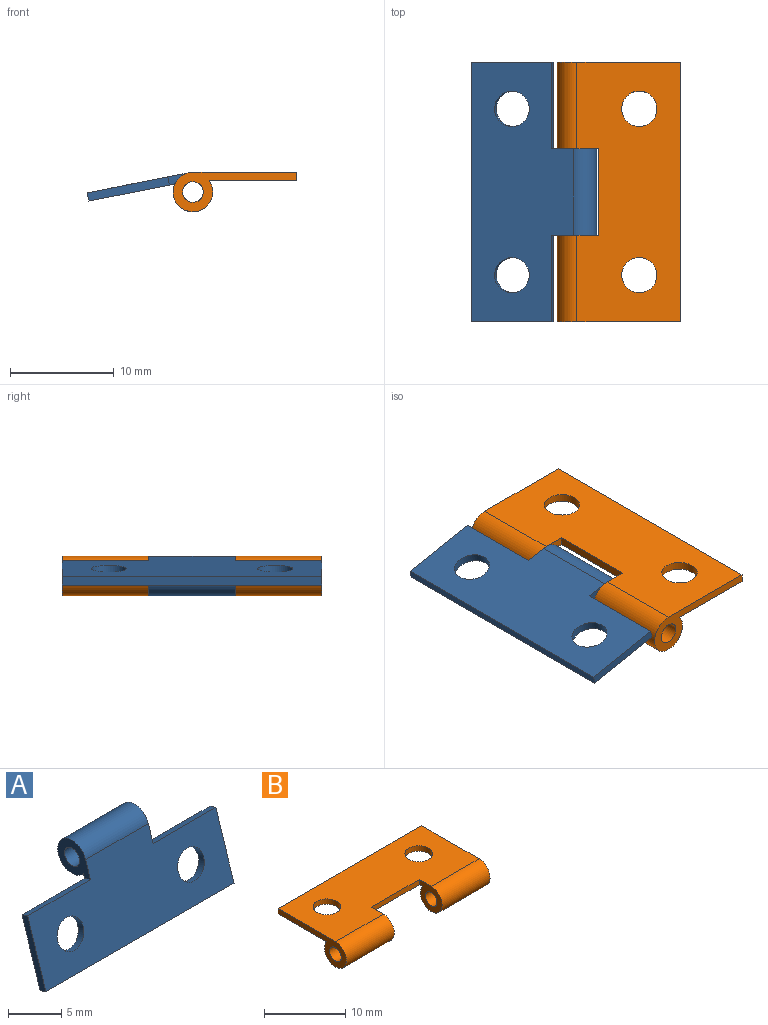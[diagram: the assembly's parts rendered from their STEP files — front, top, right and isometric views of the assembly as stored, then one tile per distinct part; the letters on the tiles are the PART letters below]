
ASSEMBLY  parts=2 mates=1
PART A: 13 faces, bbox 25x6.8x11.1 mm
  f0: cylinder r=1.9mm len=8.33mm, axis (1,0,0), area 84.4mm2, adj f1,f2,f6,f8
  f1: plane 25x8.05mm, normal (0,0.95,-0.31), area 184.1mm2, adj f0,f3,f4,f5,f6,f7,f8,f9
  f2: plane 25x9.52mm, normal (0,-0.95,0.31), area 197mm2, adj f0,f3,f4,f5,f6,f7,f8,f9
  f3: plane 7.78x3.18mm, normal (-1,0,0), area 6.3mm2, adj f1,f2,f5,f7
  f4: plane 7.78x3.18mm, normal (1,0,0), area 6.3mm2, adj f1,f2,f5,f9
  f5: plane 25x0.76mm, normal (0,-0.31,-0.95), area 20mm2, adj f1,f2,f3,f4
  f6: plane 4.35x3.8mm, normal (-1,0,0), area 9mm2, adj f0,f1,f2,f7,f10
  f7: plane 8.33x0.76mm, normal (0,0.31,0.95), area 6.7mm2, adj f1,f2,f3,f6
  f8: plane 4.35x3.8mm, normal (1,0,0), area 9mm2, adj f0,f1,f2,f9,f10
  f9: plane 8.33x0.76mm, normal (0,0.31,0.95), area 6.7mm2, adj f1,f2,f4,f8
  f10: cylinder r=1mm len=8.33mm, axis (1,0,0), area 52.4mm2, adj f6,f8
  f11: cylinder r=1.7mm len=3.48mm, axis (0,-0.95,0.31), area 8.5mm2, adj f1,f2
  f12: cylinder r=1.7mm len=3.48mm, axis (0,-0.95,0.31), area 8.5mm2, adj f1,f2
PART B: 14 faces, bbox 25x11.9x3.8 mm
  f0: plane 25x8.45mm, normal (0,0,-1), area 188.6mm2, adj f1,f2,f6,f7,f8,f9,f10,f11
  f1: cylinder r=1.9mm len=8.33mm, axis (1,0,0), area 84.4mm2, adj f0,f3,f7,f9
  f2: cylinder r=1.9mm len=8.33mm, axis (1,0,0), area 84.4mm2, adj f0,f3,f8,f10
  f3: plane 25x10mm, normal (0,0,1), area 214.4mm2, adj f1,f2,f6,f7,f8,f9,f10,f11
  f4: cylinder r=1mm len=8.33mm, axis (1,0,0), area 52.4mm2, adj f7,f9
  f5: cylinder r=1mm len=8.33mm, axis (1,0,0), area 52.4mm2, adj f8,f10
  f6: plane 25x0.8mm, normal (0,1,0), area 20mm2, adj f0,f3,f7,f8
  f7: plane 11.9x3.8mm, normal (-1,0,0), area 15.3mm2, adj f0,f1,f3,f4,f6
  f8: plane 11.9x3.8mm, normal (1,0,0), area 15.3mm2, adj f0,f2,f3,f5,f6
  f9: plane 3.99x3.8mm, normal (1,0,0), area 9mm2, adj f0,f1,f3,f4,f11
  f10: plane 3.99x3.8mm, normal (-1,0,0), area 9mm2, adj f0,f2,f3,f5,f11
  f11: plane 8.33x0.8mm, normal (0,-1,0), area 6.7mm2, adj f0,f3,f9,f10
  f12: cylinder r=1.7mm len=3.4mm, axis (0,0,1), area 8.5mm2, adj f0,f3
  f13: cylinder r=1.7mm len=3.4mm, axis (0,0,1), area 8.5mm2, adj f0,f3
PLACE A rot(axis=(-0.45,0.45,-0.77),104.9deg) t=(-82.85,83.29,-60.27)mm
PLACE B rot(axis=(0,0,-1),90deg) t=(8.18,83.29,-98.08)mm
MATE revolute B.f1 <-> A.f0  axis (0,-1,0) through (-5.24,4.17,-1.9)mm
